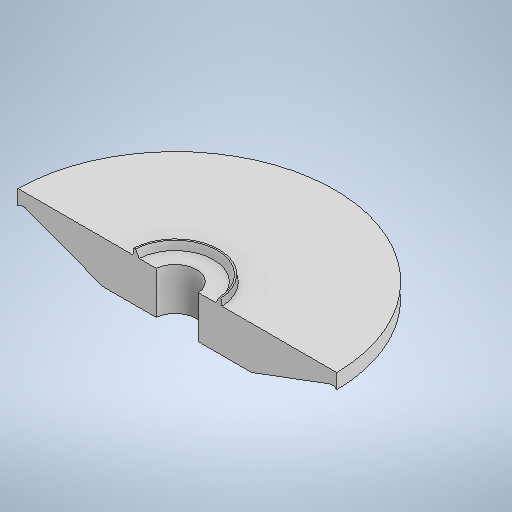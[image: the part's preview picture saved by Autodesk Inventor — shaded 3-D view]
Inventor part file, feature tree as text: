
AUTODESK INVENTOR PART (.ipt)
format: ipt  version: 2025 (Build 290162000, 162)  size: 269,312 bytes
history: native  units: mm
features: sketch x4, chamfer x1, other x1, revolve x1, fillet x1, extrude x1
ambient origin geometry x8: Origin, YZ Plane, XZ Plane, XY Plane, X Axis, Y Axis, Z Axis, Center Point
bodies: Solid1 (feature_tree), Body (feature_tree)
feature tree (9):
  chamfer  "Bottom Chamfer"  Distance=2.0mm
  other  "Centering Lip"
  revolve  "Revolution2"  [1 undecoded]
  fillet  "Fillet1"  Radius=0.3mm
  extrude  "Extrusion5"  Depth=10.0mm
  sketch  "Sketch1"  dims[d0=2.0mm]
  sketch  "Sketch4"  dims[d1=15.0mm d2=2.0mm d3=0.0mm]
  sketch  "Sketch6"  dims[d11=1.5mm d12=4.0mm d13=45.0deg d16=0.3mm d17=0.3mm]
  sketch  "Sketch7"  dims[d18=2.1mm d19=1.745329mm d20=30.0deg d21=90.0deg d27=0.3mm d28=0.7mm d29=90.0deg d30=0.3mm d31=0.1mm d32=10.0mm d33=0.0mm]
note: 1 required parameter value undecoded (feature->parameter linkage not recoverable at this tier; creation-order binding heuristic only, values carry confidence <= 0.55)
